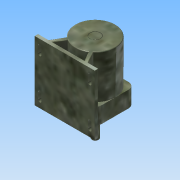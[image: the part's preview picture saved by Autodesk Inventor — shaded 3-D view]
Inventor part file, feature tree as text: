
AUTODESK INVENTOR PART (.ipt)
format: ipt  version: 2015 (Build 190159000, 159)  size: 325,632 bytes
history: native  units: mm
features: extrude x10, sketch x10, fillet x6, plane x1, chamfer x1
ambient origin geometry x8: Origin, YZ Plane, XZ Plane, XY Plane, X Axis, Y Axis, Z Axis, Center Point
bodies: 实体1 (feature_tree)
feature tree (28):
  extrude  "拉伸1"  Depth=50.0mm TaperAngle=0.0deg
  extrude  "拉伸2"  Depth=130.0mm TaperAngle=0.0deg
  extrude  "拉伸3"  Depth=30.0mm TaperAngle=0.0deg
  extrude  "拉伸4"  Depth=56.0mm TaperAngle=0.0deg
  extrude  "拉伸5"  Depth=10.0mm
  extrude  "拉伸6"  Depth=10.0mm TaperAngle=0.0deg
  fillet  "圆角1"  Radius=10.0mm
  fillet  "圆角2"  [1 undecoded]
  fillet  "圆角3"  Radius=180.0mm
  extrude  "拉伸7"  Depth=20.0mm
  fillet  "圆角4"  Radius=2.0mm
  extrude  "拉伸8"  Depth=10.0mm
  fillet  "圆角5"  Radius=15.0mm
  extrude  "拉伸9"  Depth=10.0mm
  fillet  "圆角6"  Radius=120.0mm
  plane  "工作平面1"
  extrude  "拉伸10"  Depth=30.0mm
  chamfer  "倒角1"  Distance=31.0mm
  sketch  "草图1"  dims[d0=120.0mm d1=50.0mm d2=0.0mm]
  sketch  "草图2"  dims[d3=120.0mm d4=130.0mm d5=0.0mm]
  sketch  "草图3"  dims[d6=30.0mm d7=30.0mm d8=0.0mm]
  sketch  "草图4"  dims[d9=20.0mm d10=56.0mm d11=0.0mm]
  sketch  "草图5"  dims[d12=180.0mm d13=10.0mm]
  sketch  "草图6"  dims[d14=81.384mm d15=180.0mm d16=0.0mm d17=10.0mm d18=60.0deg d19=180.0mm d20=0.0mm]
  sketch  "草图7"  dims[d21=2.0mm d22=20.0mm d23=2.0mm]
  sketch  "草图8"  dims[d24=30.0mm d25=10.0mm d26=15.0mm]
  sketch  "草图9"  dims[d27=10.0mm d28=10.0mm d29=120.0mm]
  sketch  "草图10"  dims[d30=180.0mm d31=0.0mm d32=5.0mm d33=31.0mm d34=30.0mm d35=40.0mm d36=42.0mm d37=5.0mm d38=0.0mm d39=0.5mm d40=30.0mm d41=32.0mm d42=5.0mm d43=0.0mm d44=0.5mm d45=6.0mm d46=30.0mm d47=5.0mm d48=2.5mm d49=0.0mm d50=1.0mm d51=2.0mm d52=45.0deg]
note: 1 required parameter value undecoded (feature->parameter linkage not recoverable at this tier; creation-order binding heuristic only, values carry confidence <= 0.55)
